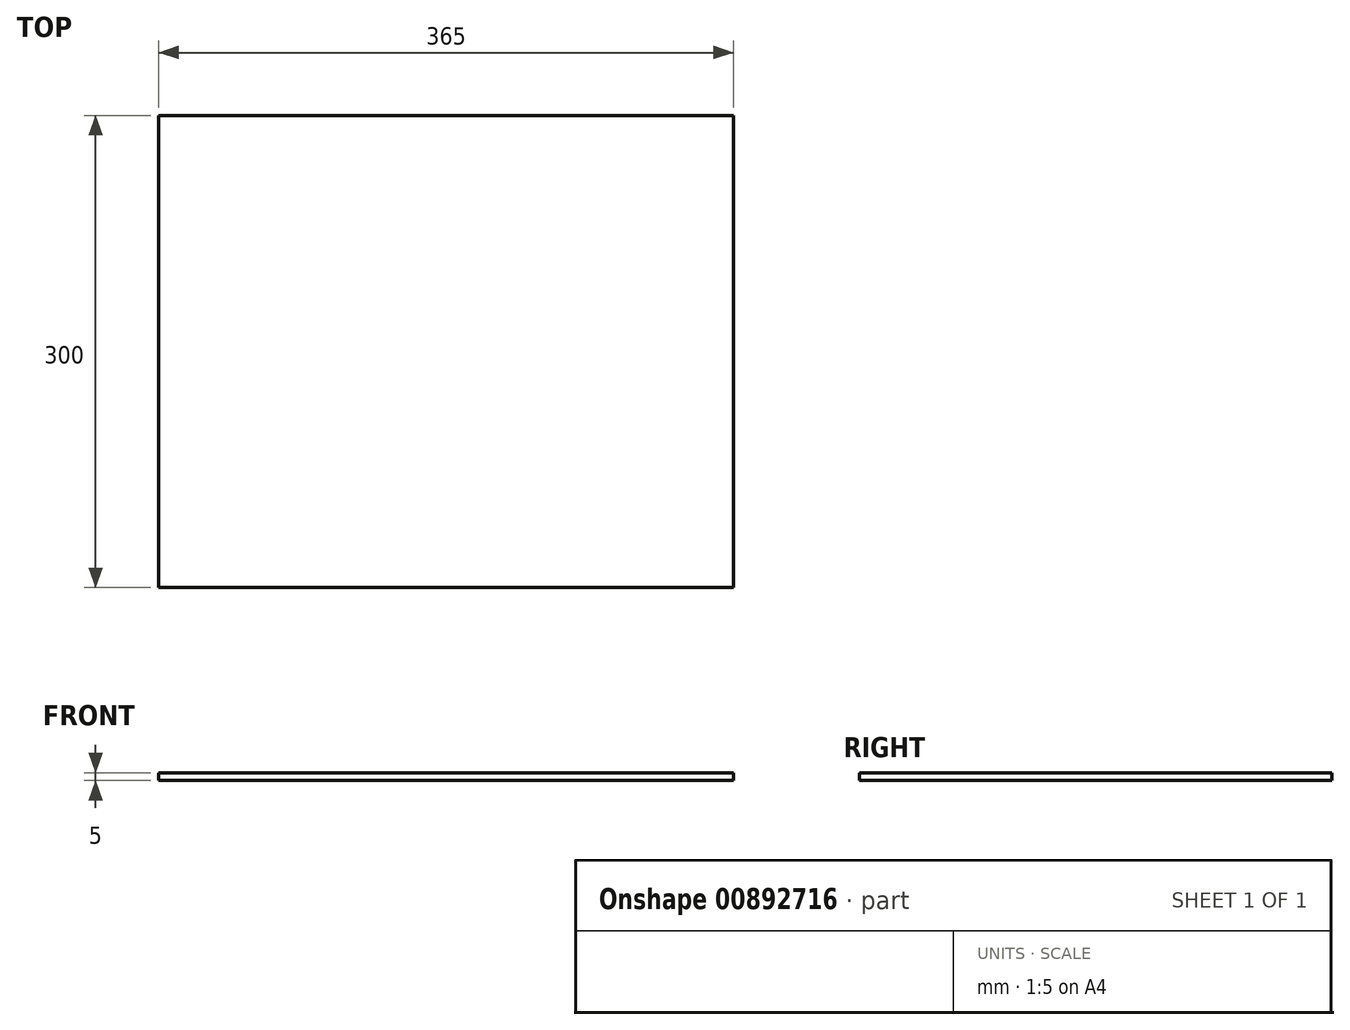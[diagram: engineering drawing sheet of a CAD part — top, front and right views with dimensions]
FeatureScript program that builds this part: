
annotation { "Feature Type Name" : "Feature", "Feature Type Description" : "" }
export const myFeature = defineFeature(function(context is Context, id is Id, definition is map)
    precondition{}
    {
        {
            var Q0;
            Q0=qCreatedBy(makeId("Top.planeOp"),FACE);
            var sketch = newSketch(context, id + "F0", { "sketchPlane" : qUnion([Q0])});
            skLineSegment(sketch, "E0.bottom", {"start": v(-182.5, 150) * mm, "end": v(182.5, 150) * mm});
            skLineSegment(sketch, "E0.top", {"start": v(-182.5, -150) * mm, "end": v(182.5, -150) * mm});
            skLineSegment(sketch, "E0.left", {"start": v(-182.5, 150) * mm, "end": v(-182.5, -150) * mm});
            skLineSegment(sketch, "E0.right", {"start": v(182.5, 150) * mm, "end": v(182.5, -150) * mm});
            skPoint(sketch, "E0.middle", {"position": v(0, 0) * mm});
            skSolve(sketch);
        }
        {
            var Q0;
            Q0=makeQuery(id+"F0.imprint","IMPRINT",FACE,{"disambiguationData":[TD([[makeQuery(id+"F0.imprint","IMPRINT",EDGE,{"derivedFrom":sQuery(id+"F0.wireOp",EDGE,"E0.bottom")}),-1.0]])]});
            extrude(context, id + "F1", {"entities" : qUnion([Q0]), "depth" : 5 * mm, "offsetDistance" : 25 * mm});
        }
    });
